# Revit family: 19302_RPSB
name_source: partatom
category: Air Terminals
revit_build: Autodesk Revit MEP 2012 (Build: 20110309_2315(x64)
units: mm (PartAtom-declared; Revit-internal decimal feet)

## types (1)
- RPSB
    Conect_Horizontal = 29 3/4"
    Conect_Vertical = 29 3/4"
    Cuello Mín-Máx Cuadrado = Desde 4"x4" a 30"x30"
    Cuello Mín-Máx Rectangular = De 5x4" a 30x29"
    Description = Rejilla para inyección o retorno
    Función = Inyección/Retorno
    Incrementos de Cuello = de 1"
    Malla = Default
    Manufacturer = INNES
    Material = Acero/Inoxidable
    Medida_Requerida_Horizontal = 30"
    Medida_Requerida_Vertical = 30"
    Model = RPSB
    Nota1 = .
    Posición de Instalación = Muro
    Tipo de Cuello = Cuadrado/Rectangular
    Type Comments = Rejilla perforada de seguridad media-baja
    URL = https://www.innes.com.mx
    Var1_H = 30"
    Var1_V = 30"
    Visible_Texto = No

## geometry (parser evidence)
native form markers: Sweep x8
no freeform markers — native parametric forms only
